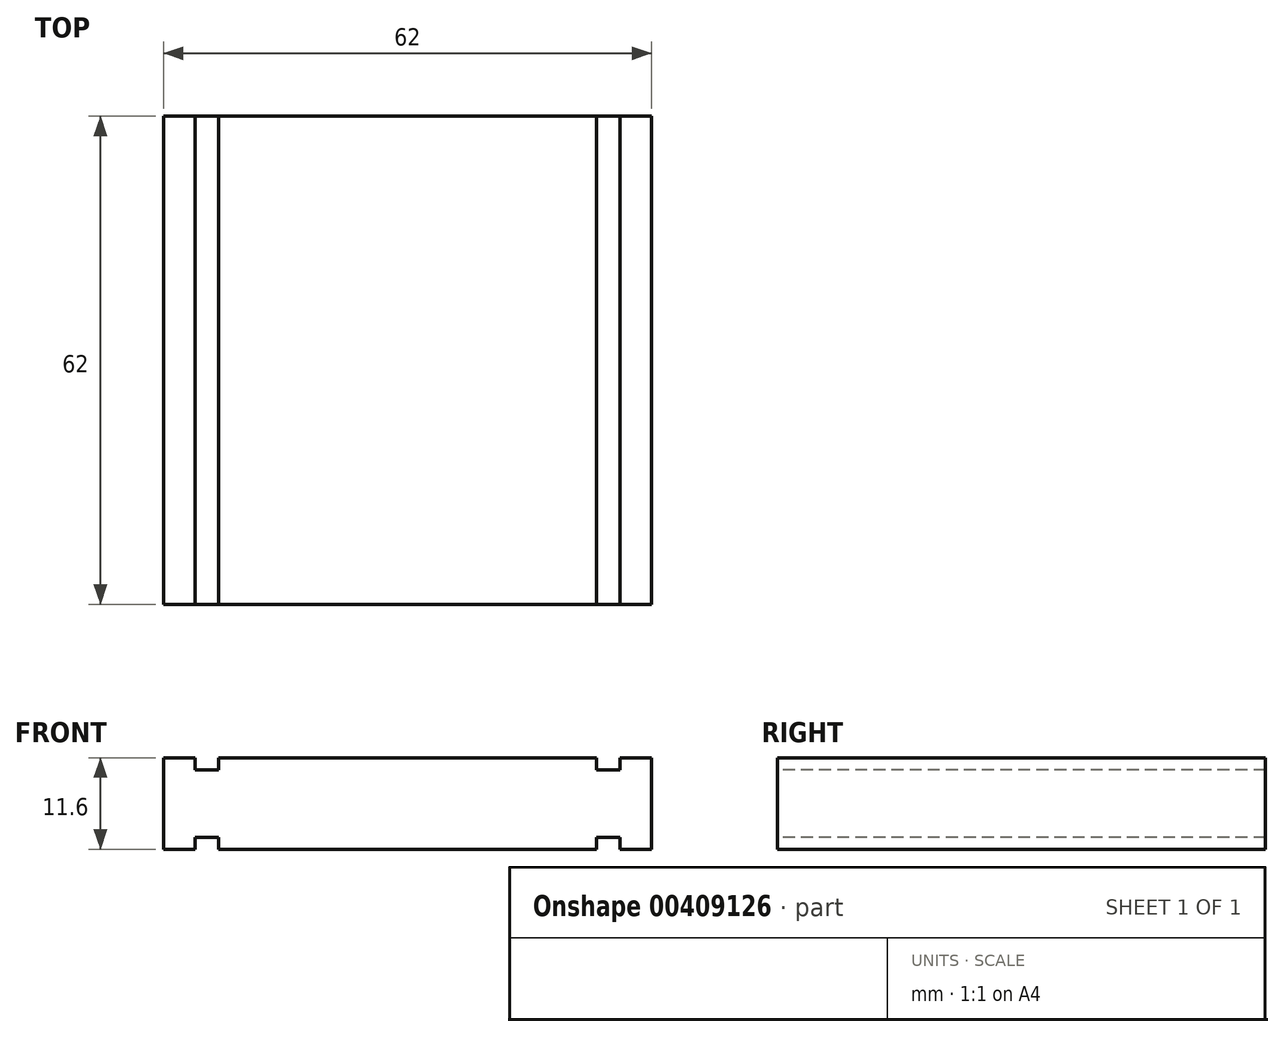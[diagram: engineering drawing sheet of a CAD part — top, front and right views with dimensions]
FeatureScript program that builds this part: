
annotation { "Feature Type Name" : "Feature", "Feature Type Description" : "" }
export const myFeature = defineFeature(function(context is Context, id is Id, definition is map)
    precondition{}
    {
        {
            var Q0;
            Q0=qCreatedBy(makeId("Top.planeOp"),FACE);
            var sketch = newSketch(context, id + "F0", { "sketchPlane" : qUnion([Q0])});
            skLineSegment(sketch, "E0.bottom", {"start": v(31, 31) * mm, "end": v(-31, 31) * mm});
            skLineSegment(sketch, "E0.top", {"start": v(31, -31) * mm, "end": v(-31, -31) * mm});
            skLineSegment(sketch, "E0.left", {"start": v(31, 31) * mm, "end": v(31, -31) * mm});
            skLineSegment(sketch, "E0.right", {"start": v(-31, 31) * mm, "end": v(-31, -31) * mm});
            skPoint(sketch, "E0.middle", {"position": v(0, 0) * mm});
            skSolve(sketch);
        }
        {
            var Q0;
            Q0 = qSketchRegion(id + "F0", true);
            extrude(context, id + "F1", {"entities" : qUnion([Q0]), "depth" : 11.6 * mm, "offsetDistance" : 25 * mm});
        }
        {
            var Q0;
            Q0=makeQuery(id+"F1.opExtrude","SWEPT_FACE",FACE,{"disambiguationData":[OSD([sQuery(id+"F0.wireOp",EDGE,"E0.top")])]});
            var sketch = newSketch(context, id + "F2", { "sketchPlane" : qUnion([Q0])});
            skLineSegment(sketch, "E1.bottom", {"start": v(27, 0) * mm, "end": v(24, 0) * mm});
            skLineSegment(sketch, "E1.top", {"start": v(27, 1.5) * mm, "end": v(24, 1.5) * mm});
            skLineSegment(sketch, "E1.left", {"start": v(27, 0) * mm, "end": v(27, 1.5) * mm});
            skLineSegment(sketch, "E1.right", {"start": v(24, 0) * mm, "end": v(24, 1.5) * mm});
            skLineSegment(sketch, "E2.bottom", {"start": v(27, 0) * mm, "end": v(31, 0) * mm});
            skLineSegment(sketch, "E2.top", {"start": v(27, 0) * mm, "end": v(31, 0) * mm});
            skLineSegment(sketch, "E2.left", {"start": v(27, 0) * mm, "end": v(27, 0) * mm});
            skLineSegment(sketch, "E2.right", {"start": v(31, 0) * mm, "end": v(31, 0) * mm});
            skLineSegment(sketch, "E3.bottom", {"start": v(27, 11.6) * mm, "end": v(24, 11.6) * mm});
            skLineSegment(sketch, "E3.top", {"start": v(27, 10.1) * mm, "end": v(24, 10.1) * mm});
            skLineSegment(sketch, "E3.left", {"start": v(27, 11.6) * mm, "end": v(27, 10.1) * mm});
            skLineSegment(sketch, "E3.right", {"start": v(24, 11.6) * mm, "end": v(24, 10.1) * mm});
            skLineSegment(sketch, "E4.bottom", {"start": v(-27, 0) * mm, "end": v(-24, 0) * mm});
            skLineSegment(sketch, "E4.top", {"start": v(-27, 1.5) * mm, "end": v(-24, 1.5) * mm});
            skLineSegment(sketch, "E4.left", {"start": v(-27, 0) * mm, "end": v(-27, 1.5) * mm});
            skLineSegment(sketch, "E4.right", {"start": v(-24, 0) * mm, "end": v(-24, 1.5) * mm});
            skLineSegment(sketch, "E5.bottom", {"start": v(-27, 11.6) * mm, "end": v(-24, 11.6) * mm});
            skLineSegment(sketch, "E5.top", {"start": v(-27, 10.1) * mm, "end": v(-24, 10.1) * mm});
            skLineSegment(sketch, "E5.left", {"start": v(-27, 11.6) * mm, "end": v(-27, 10.1) * mm});
            skLineSegment(sketch, "E5.right", {"start": v(-24, 11.6) * mm, "end": v(-24, 10.1) * mm});
            skSolve(sketch);
        }
        {
            var Q0;
            Q0=makeQuery(id+"F2.imprint","IMPRINT",FACE,{"disambiguationData":[TD([[makeQuery(id+"F2.imprint","IMPRINT",EDGE,{"derivedFrom":sQuery(id+"F2.wireOp",EDGE,"E5.bottom")}),1.0]])]});
            var Q1;
            Q1=makeQuery(id+"F2.imprint","IMPRINT",FACE,{"disambiguationData":[TD([[makeQuery(id+"F2.imprint","IMPRINT",EDGE,{"derivedFrom":sQuery(id+"F2.wireOp",EDGE,"E4.bottom")}),-1.0]])]});
            var Q2;
            Q2=makeQuery(id+"F2.imprint","IMPRINT",FACE,{"disambiguationData":[TD([[makeQuery(id+"F2.imprint","IMPRINT",EDGE,{"derivedFrom":sQuery(id+"F2.wireOp",EDGE,"E3.bottom")}),1.0]])]});
            var Q3;
            Q3=makeQuery(id+"F2.imprint","IMPRINT",FACE,{"disambiguationData":[TD([[makeQuery(id+"F2.imprint","IMPRINT",EDGE,{"derivedFrom":sQuery(id+"F2.wireOp",EDGE,"E1.bottom")}),-1.0]])]});
            extrude(context, id + "F3", {"entities" : qUnion([Q0, Q1, Q2, Q3]), "operationType" : NewBodyOperationType.REMOVE, "oppositeDirection" : true, "depth" : 62 * mm, "offsetDistance" : 25 * mm});
        }
    });
